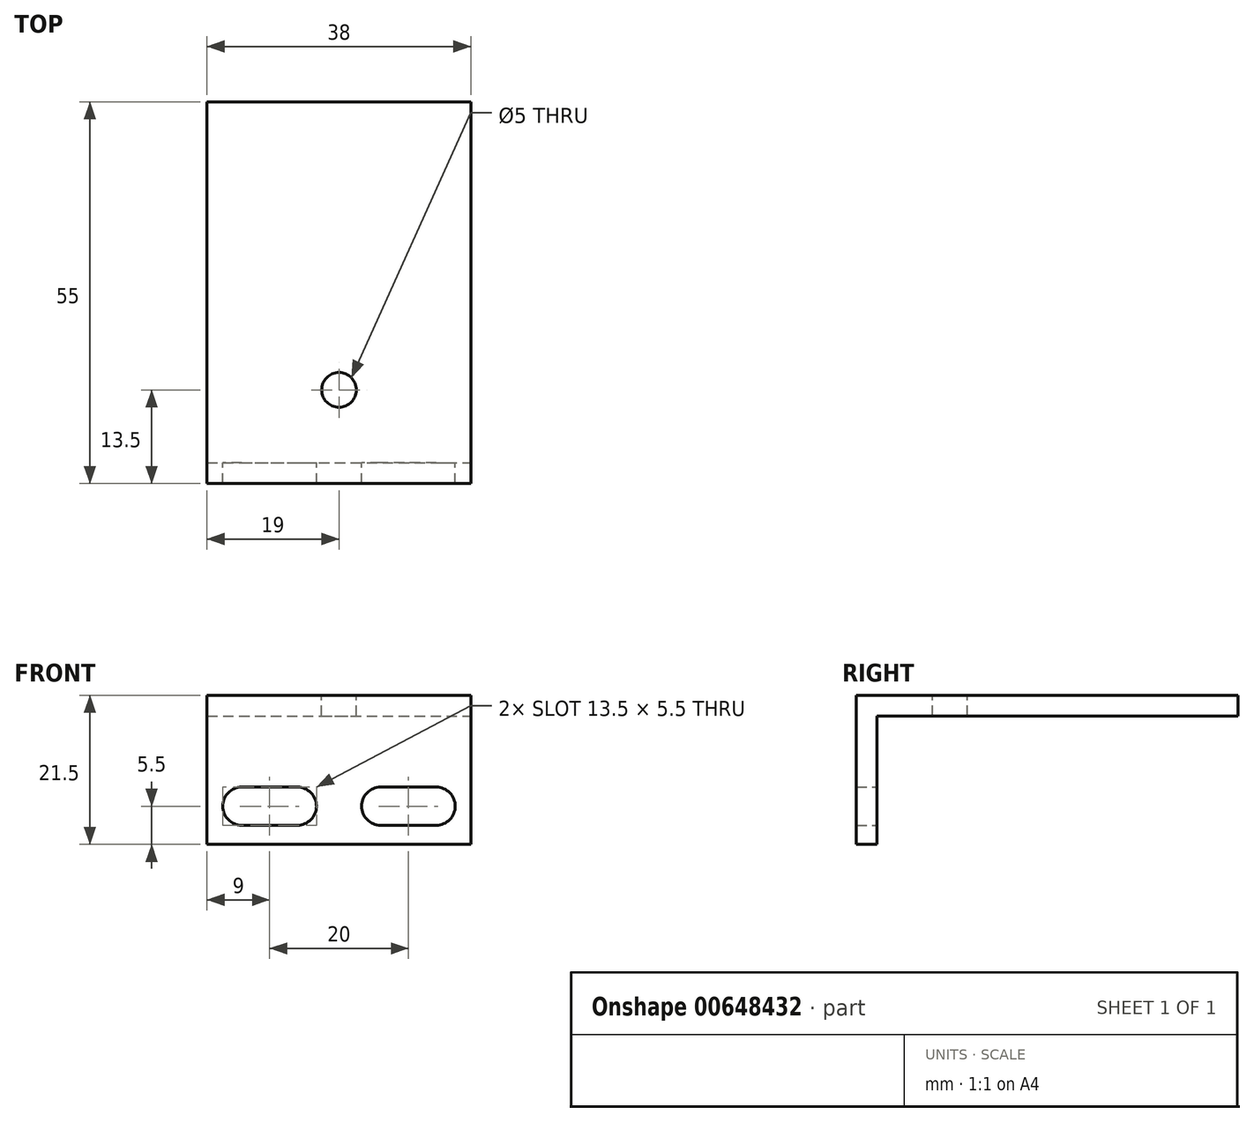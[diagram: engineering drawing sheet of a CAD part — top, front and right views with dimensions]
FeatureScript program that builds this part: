
annotation { "Feature Type Name" : "Feature", "Feature Type Description" : "" }
export const myFeature = defineFeature(function(context is Context, id is Id, definition is map)
    precondition{}
    {
        {
            var Q0;
            Q0=qCreatedBy(makeId("Front.planeOp"),FACE);
            var sketch = newSketch(context, id + "F0", { "sketchPlane" : qUnion([Q0])});
            skLineSegment(sketch, "E0.bottom", {"start": v(-19, 10.75) * mm, "end": v(19, 10.75) * mm});
            skLineSegment(sketch, "E0.top", {"start": v(-19, -10.75) * mm, "end": v(19, -10.75) * mm});
            skLineSegment(sketch, "E0.left", {"start": v(-19, 10.75) * mm, "end": v(-19, -10.75) * mm});
            skLineSegment(sketch, "E0.right", {"start": v(19, 10.75) * mm, "end": v(19, -10.75) * mm});
            skPoint(sketch, "E0.middle", {"position": v(0, 0) * mm});
            skArc(sketch, "E1", {"start": v(-14, -2.5) * mm, "mid": v(-16.75, -5.25) * mm, "end": v(-14, -8) * mm});
            skArc(sketch, "E2", {"start": v(-6, -8) * mm, "mid": v(-3.25, -5.25) * mm, "end": v(-6, -2.5) * mm});
            skLineSegment(sketch, "E3", {"start": v(-14, -2.5) * mm, "end": v(-6, -2.5) * mm});
            skLineSegment(sketch, "E4", {"start": v(-6, -8) * mm, "end": v(-14, -8) * mm});
            skLineSegment(sketch, "E5.MirrorCS", {"start": v(6, -8) * mm, "end": v(14, -8) * mm});
            skLineSegment(sketch, "E6.MirrorCS", {"start": v(14, -2.5) * mm, "end": v(6, -2.5) * mm});
            skArc(sketch, "E7.MirrorCS", {"start": v(6, -8) * mm, "mid": v(3.25, -5.25) * mm, "end": v(6, -2.5) * mm});
            skArc(sketch, "E8.MirrorCS", {"start": v(14, -2.5) * mm, "mid": v(16.75, -5.25) * mm, "end": v(14, -8) * mm});
            skSolve(sketch);
        }
        {
            var Q0;
            Q0 = qSketchRegion(id + "F0", true);
            extrude(context, id + "F1", {"entities" : qUnion([Q0]), "depth" : 3 * mm, "offsetDistance" : 25 * mm});
        }
        {
            var Q0;
            Q0=makeQuery(id+"F1.opExtrude","CAP_FACE",FACE,{"disambiguationData":[OSD([sQuery(id+"F0.wireOp",EDGE,"E0.bottom"),sQuery(id+"F0.wireOp",EDGE,"E0.top"),sQuery(id+"F0.wireOp",EDGE,"E0.left"),sQuery(id+"F0.wireOp",EDGE,"E0.right")])],"isStart":false});
            var sketch = newSketch(context, id + "F2", { "sketchPlane" : qUnion([Q0])});
            skLineSegment(sketch, "E9.bottom", {"start": v(-19, 10.75) * mm, "end": v(19, 10.75) * mm});
            skLineSegment(sketch, "E9.top", {"start": v(-19, 7.75) * mm, "end": v(19, 7.75) * mm});
            skLineSegment(sketch, "E9.left", {"start": v(-19, 10.75) * mm, "end": v(-19, 7.75) * mm});
            skLineSegment(sketch, "E9.right", {"start": v(19, 10.75) * mm, "end": v(19, 7.75) * mm});
            skSolve(sketch);
        }
        {
            var Q0;
            Q0 = qSketchRegion(id + "F2", true);
            extrude(context, id + "F3", {"entities" : qUnion([Q0]), "operationType" : NewBodyOperationType.ADD, "oppositeDirection" : true, "depth" : 55 * mm, "offsetDistance" : 25 * mm});
        }
        {
            var Q0;
            Q0=makeQuery(id+"F3.boolean.opBoolean","MERGE",FACE,{"derivedFrom":[makeQuery(id+"F1.opExtrude","SWEPT_FACE",FACE,{"disambiguationData":[OSD([sQuery(id+"F0.wireOp",EDGE,"E0.bottom")])]}),makeQuery(id+"F3.opExtrude","SWEPT_FACE",FACE,{"disambiguationData":[OSD([sQuery(id+"F2.wireOp",EDGE,"E9.bottom")])]})]});
            var sketch = newSketch(context, id + "F4", { "sketchPlane" : qUnion([Q0])});
            skCircle(sketch, "E10", {"center": v(0, 10.5) * mm, "radius": 2.5 * mm});
            skSolve(sketch);
        }
        {
            var Q0;
            Q0 = qSketchRegion(id + "F4", true);
            extrude(context, id + "F5", {"entities" : qUnion([Q0]), "operationType" : NewBodyOperationType.REMOVE, "endBound" : BoundingType.THROUGH_ALL, "oppositeDirection" : true, "depth" : 25 * mm, "offsetDistance" : 25 * mm});
        }
    });
